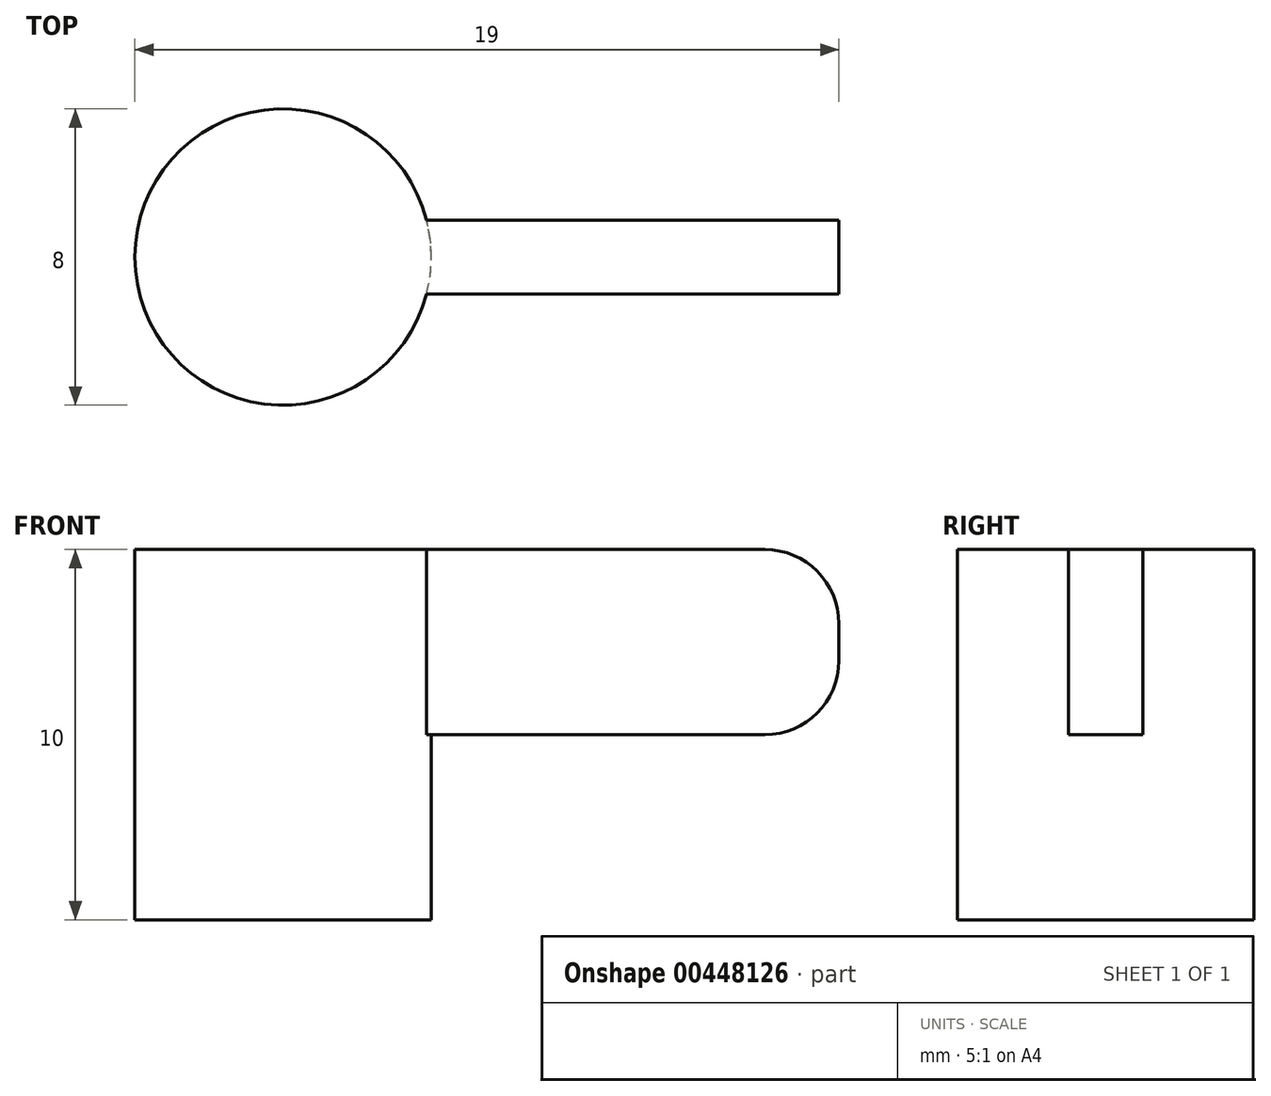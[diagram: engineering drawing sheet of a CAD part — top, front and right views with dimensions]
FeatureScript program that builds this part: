
annotation { "Feature Type Name" : "Feature", "Feature Type Description" : "" }
export const myFeature = defineFeature(function(context is Context, id is Id, definition is map)
    precondition{}
    {
        {
            var Q0;
            Q0=qCreatedBy(makeId("Top.planeOp"),FACE);
            var sketch = newSketch(context, id + "F0", { "sketchPlane" : qUnion([Q0])});
            skCircle(sketch, "E0", {"center": v(0, 0) * mm, "radius": 4 * mm});
            skSolve(sketch);
        }
        {
            var Q0;
            Q0 = qSketchRegion(id + "F0", true);
            extrude(context, id + "F1", {"entities" : qUnion([Q0]), "depth" : 10 * mm});
        }
        {
            var Q0;
            Q0=makeQuery(id+"F1.opExtrude","CAP_FACE",FACE,{"disambiguationData":[OSD([sQuery(id+"F0.wireOp",EDGE,"E0")])],"isStart":false});
            var sketch = newSketch(context, id + "F2", { "sketchPlane" : qUnion([Q0])});
            skLineSegment(sketch, "E1.bottom", {"start": v(0, 1) * mm, "end": v(15, 1) * mm});
            skLineSegment(sketch, "E1.top", {"start": v(0, -1) * mm, "end": v(15, -1) * mm});
            skLineSegment(sketch, "E1.left", {"start": v(0, 1) * mm, "end": v(0, -1) * mm});
            skLineSegment(sketch, "E1.right", {"start": v(15, 1) * mm, "end": v(15, -1) * mm});
            skPoint(sketch, "E2", {"position": v(0, 0) * mm});
            skSolve(sketch);
        }
        {
            var Q0;
            Q0 = qSketchRegion(id + "F2", true);
            extrude(context, id + "F3", {"entities" : qUnion([Q0]), "operationType" : NewBodyOperationType.ADD, "oppositeDirection" : true, "depth" : 5 * mm});
        }
        {
            var Q0;
            Q0=makeQuery(id+"F3.opExtrude","CAP_EDGE",EDGE,{"disambiguationData":[OSD([sQuery(id+"F2.wireOp",EDGE,"E1.right")])],"isStart":true});
            var Q1;
            Q1=makeQuery(id+"F3.opExtrude","CAP_EDGE",EDGE,{"disambiguationData":[OSD([sQuery(id+"F2.wireOp",EDGE,"E1.right")])],"isStart":false});
            fillet(context, id + "F4", {"entities" : qUnion([Q0, Q1]), "radius" : 2 * mm, "tangentPropagation" : true, "allowEdgeOverflow" : false});
        }
    });
